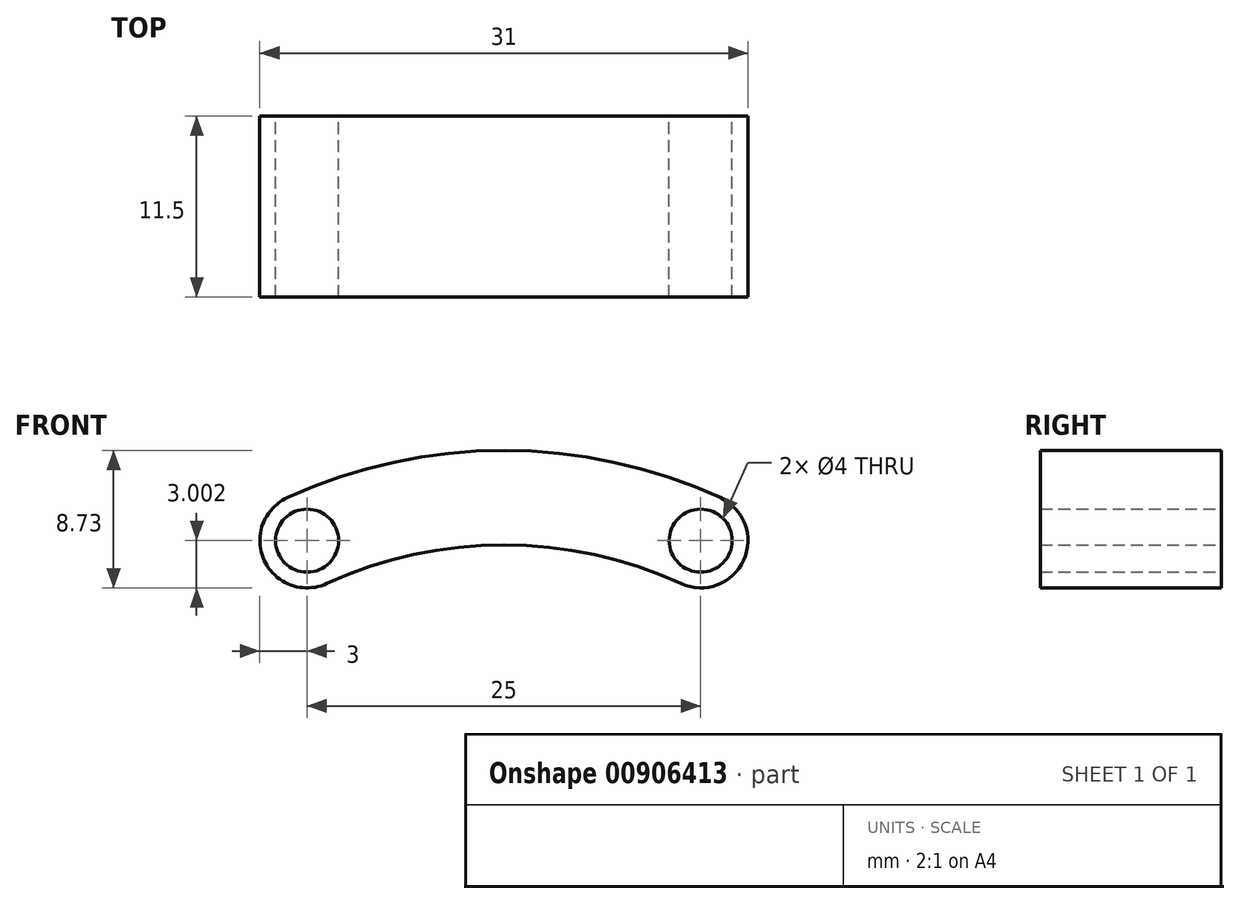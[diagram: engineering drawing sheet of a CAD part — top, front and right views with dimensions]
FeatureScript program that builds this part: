
annotation { "Feature Type Name" : "Feature", "Feature Type Description" : "" }
export const myFeature = defineFeature(function(context is Context, id is Id, definition is map)
    precondition{}
    {
        {
            var Q0;
            Q0=qCreatedBy(makeId("Front.planeOp"),FACE);
            var sketch = newSketch(context, id + "F0", { "sketchPlane" : qUnion([Q0])});
            skArc(sketch, "E0", {"start": v(13.75, 30) * mm, "mid": v(0, 33) * mm, "end": v(-13.75, 30) * mm});
            skArc(sketch, "E1.0", {"start": v(15.16, 25.89) * mm, "mid": v(0, 30) * mm, "end": v(-15.16, 25.89) * mm, "construction": true});
            skArc(sketch, "E2.0", {"start": v(11.25, 24.54) * mm, "mid": v(0, 27) * mm, "end": v(-11.25, 24.54) * mm});
            skArc(sketch, "E3", {"start": v(11.25, 24.54) * mm, "mid": v(15.23, 26.02) * mm, "end": v(13.75, 30) * mm});
            skArc(sketch, "E4", {"start": v(-13.75, 30) * mm, "mid": v(-15.23, 26.02) * mm, "end": v(-11.25, 24.54) * mm});
            skCircle(sketch, "E5", {"center": v(12.5, 27.27) * mm, "radius": 2 * mm});
            skCircle(sketch, "E6", {"center": v(-12.5, 27.27) * mm, "radius": 2 * mm});
            skLineSegment(sketch, "E7", {"start": v(0, 36.98) * mm, "end": v(0, 0) * mm, "construction": true});
            skSolve(sketch);
        }
        {
            var Q0;
            Q0=qSketchRegion(id+"F0",true);
            extrude(context, id + "F1", {"entities" : qUnion([Q0]), "depth" : 11.5 * mm, "offsetDistance" : 25 * mm});
        }
    });
